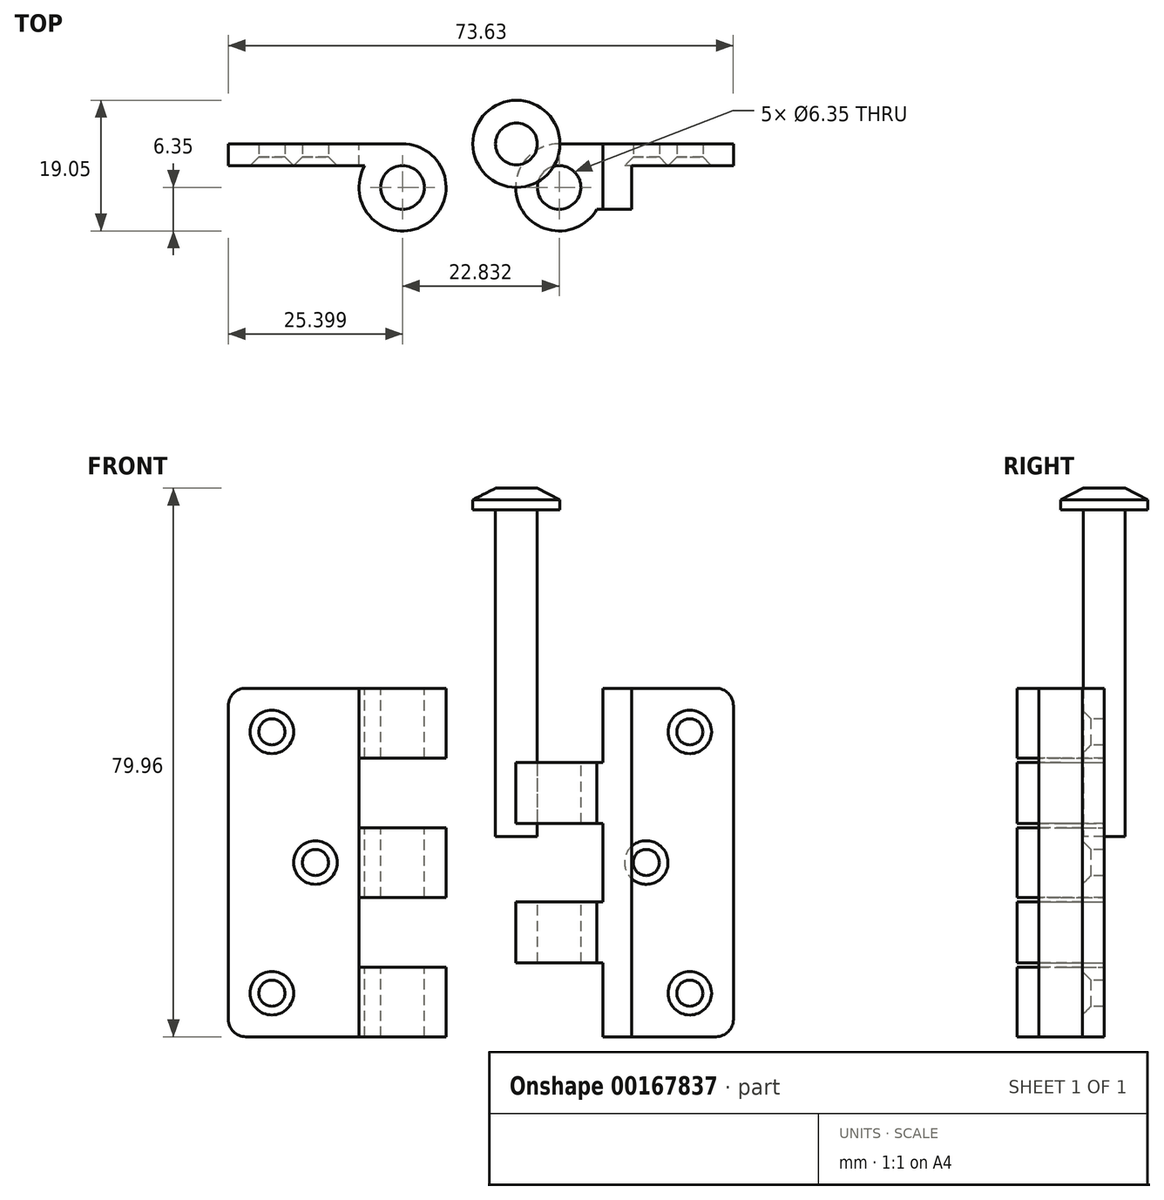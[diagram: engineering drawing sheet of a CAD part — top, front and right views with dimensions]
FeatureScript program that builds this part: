
annotation { "Feature Type Name" : "Feature", "Feature Type Description" : "" }
export const myFeature = defineFeature(function(context is Context, id is Id, definition is map)
    precondition{}
    {
        {
            var Q0;
            Q0=qCreatedBy(makeId("Front.planeOp"),FACE);
            var sketch = newSketch(context, id + "F0", { "sketchPlane" : qUnion([Q0])});
            skLineSegment(sketch, "E0.bottom", {"start": v(-44.61, 38.03) * mm, "end": v(-19.21, 38.03) * mm});
            skLineSegment(sketch, "E0.top", {"start": v(-44.61, -12.77) * mm, "end": v(-19.21, -12.77) * mm});
            skLineSegment(sketch, "E0.left", {"start": v(-44.61, 38.03) * mm, "end": v(-44.61, -12.77) * mm});
            skLineSegment(sketch, "E0.right", {"start": v(-19.21, 38.03) * mm, "end": v(-19.21, -12.77) * mm});
            skSolve(sketch);
        }
        {
            var Q0;
            Q0=qSketchRegion(id+"F0",true);
            extrude(context, id + "F1", {"entities" : qUnion([Q0]), "depth" : 3.17 * mm});
        }
        {
            var Q0;
            Q0=makeQuery(id+"F1.opExtrude","SWEPT_FACE",FACE,{"disambiguationData":[OSD([sQuery(id+"F0.wireOp",EDGE,"E0.bottom")])]});
            var sketch = newSketch(context, id + "F2", { "sketchPlane" : qUnion([Q0])});
            skCircle(sketch, "E1", {"center": v(-19.21, -6.35) * mm, "radius": 6.35 * mm});
            skCircle(sketch, "E2", {"center": v(-19.21, -6.35) * mm, "radius": 3.18 * mm});
            skSolve(sketch);
        }
        {
            var Q0;
            {var subQ5=sQuery(id+"F2.wireOp",EDGE,"E2");Q0=makeQuery(id+"F2.imprint","IMPRINT",FACE,{"disambiguationData":[TD([[makeQuery(id+"F2.imprint","IMPRINT",EDGE,{"derivedFrom":subQ5}),-1.0]])]});}
            var Q1;
            {var subQ1=sQuery(id+"F0.wireOp",EDGE,"E0.bottom");var subQ2=makeQuery(id+"F1.opExtrude","SWEPT_EDGE",EDGE,{"disambiguationData":[OSD([subQ1,sQuery(id+"F0.wireOp",EDGE,"E0.right")])]});Q1=makeQuery(id+"F2.imprint","IMPRINT",FACE,{"disambiguationData":[TD([[makeQuery(id+"F2.imprint","IMPRINT",EDGE,{"derivedFrom":subQ2}),1.0]])]});}
            var Q2;
            Q2=makeQuery(id+"F1.opExtrude","SWEPT_FACE",FACE,{"disambiguationData":[OSD([sQuery(id+"F0.wireOp",EDGE,"E0.top")])]});
            extrude(context, id + "F3", {"entities" : qUnion([Q0, Q1]), "operationType" : NewBodyOperationType.ADD, "endBound" : BoundingType.UP_TO_SURFACE, "oppositeDirection" : true, "endBoundEntityFace" : qUnion([Q2]), "depth" : 25.4 * mm});
        }
        {
            var Q0;
            Q0=makeQuery(id+"F1.opExtrude","CAP_FACE",FACE,{"disambiguationData":[OSD([sQuery(id+"F0.wireOp",EDGE,"E0.bottom"),sQuery(id+"F0.wireOp",EDGE,"E0.top"),sQuery(id+"F0.wireOp",EDGE,"E0.left"),sQuery(id+"F0.wireOp",EDGE,"E0.right")])],"isStart":false});
            var sketch = newSketch(context, id + "F4", { "sketchPlane" : qUnion([Q0])});
            skLineSegment(sketch, "E3", {"start": v(-34.66, 38.03) * mm, "end": v(-34.66, -12.77) * mm, "construction": true});
            skLineSegment(sketch, "E4", {"start": v(-24.7, 12.63) * mm, "end": v(-44.61, 12.63) * mm, "construction": true});
            skLineSegment(sketch, "E5", {"start": v(-24.7, -6.42) * mm, "end": v(-44.61, -6.42) * mm, "construction": true});
            skLineSegment(sketch, "E6", {"start": v(-24.7, 31.68) * mm, "end": v(-44.61, 31.68) * mm, "construction": true});
            skPoint(sketch, "E7", {"position": v(-38.26, 31.68) * mm});
            skPoint(sketch, "E8", {"position": v(-31.91, 12.63) * mm});
            skPoint(sketch, "E9", {"position": v(-38.26, -6.42) * mm});
            skSolve(sketch);
        }
        {
            var Q0;
            Q0=makeQuery(id+"F1.opExtrude","SWEPT_EDGE",EDGE,{"disambiguationData":[OSD([sQuery(id+"F0.wireOp",EDGE,"E0.bottom"),sQuery(id+"F0.wireOp",EDGE,"E0.left")])]});
            var Q1;
            Q1=makeQuery(id+"F1.opExtrude","SWEPT_EDGE",EDGE,{"disambiguationData":[OSD([sQuery(id+"F0.wireOp",EDGE,"E0.top"),sQuery(id+"F0.wireOp",EDGE,"E0.left")])]});
            fillet(context, id + "F5", {"entities" : qUnion([Q0, Q1]), "radius" : 2.54 * mm, "tangentPropagation" : true, "allowEdgeOverflow" : false});
        }
        {
            var Q0;
            Q0=makeQuery(id+"F0.imprint","IMPRINT",FACE,{"disambiguationData":[TD([[makeQuery(id+"F0.imprint","IMPRINT",EDGE,{"derivedFrom":sQuery(id+"F0.wireOp",EDGE,"E0.bottom")}),-1.0]])]});
            var sketch = newSketch(context, id + "F6", { "sketchPlane" : qUnion([Q0])});
            skLineSegment(sketch, "E10", {"start": v(-25.56, -2.61) * mm, "end": v(-12.86, -2.61) * mm});
            skLineSegment(sketch, "E11", {"start": v(-12.86, -2.61) * mm, "end": v(-12.86, 7.55) * mm});
            skLineSegment(sketch, "E12", {"start": v(-12.86, 7.55) * mm, "end": v(-25.56, 7.55) * mm});
            skLineSegment(sketch, "E13", {"start": v(-25.56, 7.55) * mm, "end": v(-25.56, -2.61) * mm});
            skLineSegment(sketch, "E14", {"start": v(-25.56, 17.7) * mm, "end": v(-12.86, 17.7) * mm});
            skLineSegment(sketch, "E15", {"start": v(-12.86, 17.7) * mm, "end": v(-12.86, 27.87) * mm});
            skLineSegment(sketch, "E16", {"start": v(-12.86, 27.87) * mm, "end": v(-25.56, 27.87) * mm});
            skLineSegment(sketch, "E17", {"start": v(-25.56, 27.87) * mm, "end": v(-25.56, 17.7) * mm});
            skPoint(sketch, "E18", {"position": v(-19.21, -2.61) * mm});
            skLineSegment(sketch, "E19", {"start": v(-19.21, 27.87) * mm, "end": v(-19.21, 38.03) * mm});
            skLineSegment(sketch, "E20", {"start": v(-19.21, 17.7) * mm, "end": v(-19.21, 7.55) * mm});
            skLineSegment(sketch, "E21", {"start": v(-19.21, -2.61) * mm, "end": v(-19.21, -12.77) * mm});
            skLineSegment(sketch, "E22", {"start": v(-12.86, 17.7) * mm, "end": v(-12.86, 7.55) * mm});
            skLineSegment(sketch, "E23", {"start": v(-25.56, 7.55) * mm, "end": v(-25.56, 17.7) * mm});
            skLineSegment(sketch, "E24", {"start": v(-25.56, 27.87) * mm, "end": v(-25.56, 38.04) * mm});
            skLineSegment(sketch, "E25", {"start": v(-25.56, 38.04) * mm, "end": v(-12.86, 38.03) * mm});
            skLineSegment(sketch, "E26", {"start": v(-12.86, 38.03) * mm, "end": v(-12.86, 27.87) * mm});
            skLineSegment(sketch, "E27", {"start": v(-12.86, -2.61) * mm, "end": v(-12.86, -12.77) * mm});
            skLineSegment(sketch, "E28", {"start": v(-12.86, -12.77) * mm, "end": v(-25.56, -12.77) * mm});
            skLineSegment(sketch, "E29", {"start": v(-25.56, -12.77) * mm, "end": v(-25.56, -2.61) * mm});
            skSolve(sketch);
        }
        {
            var Q0;
            {var subQ0=sQuery(id+"F6.wireOp",EDGE,"E17");Q0=makeQuery(id+"F6.imprint","IMPRINT",FACE,{"disambiguationData":[TD([[makeQuery(id+"F6.imprint","IMPRINT",EDGE,{"derivedFrom":subQ0}),1.0]])]});}
            var Q1;
            {var subQ0=sQuery(id+"F6.wireOp",EDGE,"E15");Q1=makeQuery(id+"F6.imprint","IMPRINT",FACE,{"disambiguationData":[TD([[makeQuery(id+"F6.imprint","IMPRINT",EDGE,{"derivedFrom":subQ0}),1.0]])]});}
            var Q2;
            {var subQ0=sQuery(id+"F6.wireOp",EDGE,"E13");Q2=makeQuery(id+"F6.imprint","IMPRINT",FACE,{"disambiguationData":[TD([[makeQuery(id+"F6.imprint","IMPRINT",EDGE,{"derivedFrom":subQ0}),1.0]])]});}
            var Q3;
            {var subQ0=sQuery(id+"F6.wireOp",EDGE,"E11");Q3=makeQuery(id+"F6.imprint","IMPRINT",FACE,{"disambiguationData":[TD([[makeQuery(id+"F6.imprint","IMPRINT",EDGE,{"derivedFrom":subQ0}),1.0]])]});}
            extrude(context, id + "F7", {"entities" : qUnion([Q0, Q1, Q2, Q3]), "operationType" : NewBodyOperationType.REMOVE, "depth" : 25.4 * mm});
        }
        {
            var Q0;
            Q0=qCreatedBy(makeId("Front.planeOp"),FACE);
            var sketch = newSketch(context, id + "F8", { "sketchPlane" : qUnion([Q0])});
            skLineSegment(sketch, "E30.bottom", {"start": v(3.62, 38.03) * mm, "end": v(29.02, 38.03) * mm});
            skLineSegment(sketch, "E30.top", {"start": v(3.62, -12.77) * mm, "end": v(29.02, -12.77) * mm});
            skLineSegment(sketch, "E30.left", {"start": v(3.62, 38.03) * mm, "end": v(3.62, -12.77) * mm});
            skLineSegment(sketch, "E30.right", {"start": v(29.02, 38.03) * mm, "end": v(29.02, -12.77) * mm});
            skSolve(sketch);
        }
        {
            var Q0;
            Q0=qSketchRegion(id+"F8",true);
            extrude(context, id + "F9", {"entities" : qUnion([Q0]), "depth" : 3.17 * mm});
        }
        {
            var Q0;
            Q0=makeQuery(id+"F9.opExtrude","SWEPT_FACE",FACE,{"disambiguationData":[OSD([sQuery(id+"F8.wireOp",EDGE,"E30.bottom")])]});
            var sketch = newSketch(context, id + "F10", { "sketchPlane" : qUnion([Q0])});
            skCircle(sketch, "E31", {"center": v(3.62, -6.35) * mm, "radius": 6.35 * mm});
            skLineSegment(sketch, "E32", {"start": v(-33.9, -6.35) * mm, "end": v(23.07, -6.35) * mm, "construction": true});
            skCircle(sketch, "E33", {"center": v(3.62, -6.35) * mm, "radius": 3.18 * mm});
            skPoint(sketch, "E34.endSnap0", {"position": v(16.32, -3.18) * mm});
            skLineSegment(sketch, "E35", {"start": v(9.12, -3.18) * mm, "end": v(14.2, -3.18) * mm});
            skLineSegment(sketch, "E36", {"start": v(14.2, -3.18) * mm, "end": v(14.2, -9.53) * mm});
            skLineSegment(sketch, "E37", {"start": v(14.2, -9.53) * mm, "end": v(9.12, -9.53) * mm});
            skArc(sketch, "E38", {"start": v(9.12, -9.53) * mm, "mid": v(9.97, -6.35) * mm, "end": v(9.12, -3.17) * mm});
            skSolve(sketch);
        }
        {
            var Q0;
            {var subQ5=sQuery(id+"F10.wireOp",EDGE,"E33");Q0=makeQuery(id+"F10.imprint","IMPRINT",FACE,{"disambiguationData":[TD([[makeQuery(id+"F10.imprint","IMPRINT",EDGE,{"derivedFrom":subQ5}),-1.0]])]});}
            var Q1;
            {var subQ1=sQuery(id+"F8.wireOp",EDGE,"E30.bottom");var subQ2=makeQuery(id+"F9.opExtrude","SWEPT_EDGE",EDGE,{"disambiguationData":[OSD([subQ1,sQuery(id+"F8.wireOp",EDGE,"E30.left")])]});Q1=makeQuery(id+"F10.imprint","IMPRINT",FACE,{"disambiguationData":[TD([[makeQuery(id+"F10.imprint","IMPRINT",EDGE,{"derivedFrom":subQ2}),-1.0]])]});}
            var Q2;
            {var subQ0=sQuery(id+"F10.wireOp",EDGE,"E35");Q2=makeQuery(id+"F10.imprint","IMPRINT",FACE,{"disambiguationData":[TD([[makeQuery(id+"F10.imprint","IMPRINT",EDGE,{"derivedFrom":subQ0}),-1.0]])]});}
            var Q3;
            Q3=makeQuery(id+"F9.opExtrude","SWEPT_FACE",FACE,{"disambiguationData":[OSD([sQuery(id+"F8.wireOp",EDGE,"E30.top")])]});
            extrude(context, id + "F11", {"entities" : qUnion([Q0, Q1, Q2]), "operationType" : NewBodyOperationType.ADD, "endBound" : BoundingType.UP_TO_SURFACE, "oppositeDirection" : true, "endBoundEntityFace" : qUnion([Q3]), "depth" : 25.4 * mm});
        }
        {
            var Q0;
            Q0=makeQuery(id+"F9.opExtrude","CAP_FACE",FACE,{"disambiguationData":[OSD([sQuery(id+"F8.wireOp",EDGE,"E30.bottom"),sQuery(id+"F8.wireOp",EDGE,"E30.top"),sQuery(id+"F8.wireOp",EDGE,"E30.left"),sQuery(id+"F8.wireOp",EDGE,"E30.right")])],"isStart":true});
            var sketch = newSketch(context, id + "F12", { "sketchPlane" : qUnion([Q0])});
            skLineSegment(sketch, "E39", {"start": v(-9.97, 27.23) * mm, "end": v(2.73, 27.23) * mm});
            skLineSegment(sketch, "E40", {"start": v(2.73, 27.23) * mm, "end": v(2.73, 38.03) * mm});
            skLineSegment(sketch, "E41", {"start": v(2.73, 38.03) * mm, "end": v(-9.97, 38.03) * mm});
            skLineSegment(sketch, "E42", {"start": v(-9.97, 27.23) * mm, "end": v(-9.97, 38.03) * mm});
            skLineSegment(sketch, "E43", {"start": v(-9.97, 27.23) * mm, "end": v(-9.97, -12.77) * mm});
            skLineSegment(sketch, "E44", {"start": v(-9.97, -12.77) * mm, "end": v(2.73, -12.77) * mm});
            skLineSegment(sketch, "E45", {"start": v(2.73, -12.77) * mm, "end": v(2.73, 27.23) * mm});
            skLineSegment(sketch, "E46", {"start": v(2.73, 18.34) * mm, "end": v(-9.97, 18.34) * mm});
            skLineSegment(sketch, "E47", {"start": v(-9.97, 6.91) * mm, "end": v(2.73, 6.91) * mm});
            skLineSegment(sketch, "E48", {"start": v(-9.97, -1.98) * mm, "end": v(2.73, -1.98) * mm});
            skSolve(sketch);
        }
        {
            var Q0;
            {var subQ0=sQuery(id+"F12.wireOp",EDGE,"E40");Q0=makeQuery(id+"F12.imprint","IMPRINT",FACE,{"disambiguationData":[TD([[makeQuery(id+"F12.imprint","IMPRINT",EDGE,{"derivedFrom":subQ0}),1.0]])]});}
            var Q1;
            {var subQ0=sQuery(id+"F12.wireOp",EDGE,"E42");Q1=makeQuery(id+"F12.imprint","IMPRINT",FACE,{"disambiguationData":[TD([[makeQuery(id+"F12.imprint","IMPRINT",EDGE,{"derivedFrom":subQ0}),-1.0]])]});}
            var Q2;
            {var subQ0=sQuery(id+"F12.wireOp",EDGE,"E46");var subQ1=sQuery(id+"F12.wireOp",EDGE,"E43");var subQ2=makeQuery(id+"F12.imprint","INTERSECT",VERTEX,{"derivedFrom":[subQ1,subQ0]});Q2=makeQuery(id+"F12.imprint","IMPRINT",FACE,{"disambiguationData":[TD([[makeQuery(id+"F12.imprint","IMPRINT",EDGE,{"disambiguationData":[TD([[subQ2,-1.0]])],"derivedFrom":subQ1}),1.0]])]});}
            var Q3;
            {var subQ0=sQuery(id+"F12.wireOp",EDGE,"E46");var subQ1=sQuery(id+"F12.wireOp",EDGE,"E45");var subQ2=makeQuery(id+"F12.imprint","INTERSECT",VERTEX,{"derivedFrom":[subQ1,subQ0]});Q3=makeQuery(id+"F12.imprint","IMPRINT",FACE,{"disambiguationData":[TD([[makeQuery(id+"F12.imprint","IMPRINT",EDGE,{"disambiguationData":[TD([[subQ2,1.0]])],"derivedFrom":subQ1}),1.0]])]});}
            var Q4;
            {var subQ0=sQuery(id+"F12.wireOp",EDGE,"E44");var subQ3=sQuery(id+"F12.wireOp",EDGE,"E45");var subQ4=makeQuery(id+"F12.imprint","INTERSECT",VERTEX,{"derivedFrom":[subQ0,subQ3]});Q4=makeQuery(id+"F12.imprint","IMPRINT",FACE,{"disambiguationData":[TD([[makeQuery(id+"F12.imprint","IMPRINT",EDGE,{"disambiguationData":[TD([[subQ4,1.0]])],"derivedFrom":subQ0}),1.0]])]});}
            var Q5;
            {var subQ1=sQuery(id+"F12.wireOp",EDGE,"E43");var subQ3=sQuery(id+"F12.wireOp",EDGE,"E48");var subQ4=makeQuery(id+"F12.imprint","INTERSECT",VERTEX,{"derivedFrom":[subQ1,subQ3]});Q5=makeQuery(id+"F12.imprint","IMPRINT",FACE,{"disambiguationData":[TD([[makeQuery(id+"F12.imprint","IMPRINT",EDGE,{"disambiguationData":[TD([[subQ4,-1.0]])],"derivedFrom":subQ3}),-1.0]])]});}
            extrude(context, id + "F13", {"entities" : qUnion([Q0, Q1, Q2, Q3, Q4, Q5]), "operationType" : NewBodyOperationType.REMOVE, "oppositeDirection" : true, "depth" : 25.4 * mm});
        }
        {
            var Q0;
            Q0=qCreatedBy(makeId("Front.planeOp"),FACE);
            var sketch = newSketch(context, id + "F14", { "sketchPlane" : qUnion([Q0])});
            skLineSegment(sketch, "E49", {"start": v(-5.65, 64.02) * mm, "end": v(-5.65, 16.4) * mm});
            skLineSegment(sketch, "E50", {"start": v(-5.65, 16.4) * mm, "end": v(-2.6, 16.4) * mm});
            skLineSegment(sketch, "E51", {"start": v(-2.6, 16.4) * mm, "end": v(-2.6, 67.2) * mm});
            skLineSegment(sketch, "E52", {"start": v(-2.6, 67.2) * mm, "end": v(-5.65, 67.2) * mm});
            skLineSegment(sketch, "E53", {"start": v(-5.65, 67.2) * mm, "end": v(-8.96, 65.52) * mm});
            skLineSegment(sketch, "E54", {"start": v(-8.96, 65.52) * mm, "end": v(-8.96, 64.02) * mm});
            skLineSegment(sketch, "E55", {"start": v(-8.96, 64.02) * mm, "end": v(-5.65, 64.02) * mm});
            skSolve(sketch);
        }
        {
            var Q0;
            Q0=qSketchRegion(id+"F14",true);
            var Q1;
            Q1=sQuery(id+"F14.wireOp",EDGE,"E51");
            revolve(context, id + "F15", {"entities" : qUnion([Q0]), "axis" : qUnion([Q1]), "revolveType" : RevolveType.FULL});
        }
        {
            var Q0;
            Q0=makeQuery(id+"F9.opExtrude","CAP_FACE",FACE,{"disambiguationData":[OSD([sQuery(id+"F8.wireOp",EDGE,"E30.bottom"),sQuery(id+"F8.wireOp",EDGE,"E30.top"),sQuery(id+"F8.wireOp",EDGE,"E30.left"),sQuery(id+"F8.wireOp",EDGE,"E30.right")])],"isStart":false});
            var sketch = newSketch(context, id + "F16", { "sketchPlane" : qUnion([Q0])});
            skLineSegment(sketch, "E56", {"start": v(21.6, 38.03) * mm, "end": v(21.6, -12.77) * mm, "construction": true});
            skLineSegment(sketch, "E57", {"start": v(9.97, 12.63) * mm, "end": v(29.02, 12.63) * mm, "construction": true});
            skPoint(sketch, "E58", {"position": v(16.32, 12.63) * mm});
            skPoint(sketch, "E59", {"position": v(22.67, 31.68) * mm});
            skPoint(sketch, "E60", {"position": v(22.67, -6.42) * mm});
            skSolve(sketch);
        }
        {
            var Q0;
            Q0=sQuery(id+"F4.wireOp",VERTEX,"E7");
            var Q1;
            Q1=sQuery(id+"F4.wireOp",VERTEX,"E8");
            var Q2;
            Q2=sQuery(id+"F4.wireOp",VERTEX,"E9");
            var Q3;
            Q3=makeQuery(id+"F1.opExtrude","SWEPT_BODY",BODY,{"disambiguationData":[OSD([sQuery(id+"F0.wireOp",EDGE,"E0.bottom"),sQuery(id+"F0.wireOp",EDGE,"E0.top"),sQuery(id+"F0.wireOp",EDGE,"E0.left"),sQuery(id+"F0.wireOp",EDGE,"E0.right")])]});
            hole(context, id + "F17", {"style" : HoleStyle.C_SINK, "endStyle" : HoleEndStyle.THROUGH, "holeDiameter" : 3.8 * mm, "cSinkDiameter" : 6.35 * mm, "cSinkAngle" : 90 * degree, "locations" : qUnion([Q0, Q1, Q2]), "scope" : qUnion([Q3]), "isTappedThrough" : true});
        }
        {
            var Q0;
            Q0=sQuery(id+"F16.wireOp",VERTEX,"E59");
            var Q1;
            Q1=sQuery(id+"F16.wireOp",VERTEX,"E58");
            var Q2;
            Q2=sQuery(id+"F16.wireOp",VERTEX,"E60");
            var Q3;
            Q3=makeQuery(id+"F9.opExtrude","SWEPT_BODY",BODY,{"disambiguationData":[OSD([sQuery(id+"F8.wireOp",EDGE,"E30.bottom"),sQuery(id+"F8.wireOp",EDGE,"E30.top"),sQuery(id+"F8.wireOp",EDGE,"E30.left"),sQuery(id+"F8.wireOp",EDGE,"E30.right")])]});
            hole(context, id + "F18", {"style" : HoleStyle.C_SINK, "endStyle" : HoleEndStyle.THROUGH, "holeDiameter" : 3.8 * mm, "cSinkDiameter" : 6.35 * mm, "cSinkAngle" : 90 * degree, "locations" : qUnion([Q0, Q1, Q2]), "scope" : qUnion([Q3]), "isTappedThrough" : true});
        }
        {
            var Q0;
            Q0=makeQuery(id+"F9.opExtrude","SWEPT_EDGE",EDGE,{"disambiguationData":[OSD([sQuery(id+"F8.wireOp",EDGE,"E30.bottom"),sQuery(id+"F8.wireOp",EDGE,"E30.right")])]});
            var Q1;
            Q1=makeQuery(id+"F9.opExtrude","SWEPT_EDGE",EDGE,{"disambiguationData":[OSD([sQuery(id+"F8.wireOp",EDGE,"E30.top"),sQuery(id+"F8.wireOp",EDGE,"E30.right")])]});
            fillet(context, id + "F19", {"entities" : qUnion([Q0, Q1]), "radius" : 2.54 * mm, "tangentPropagation" : true, "allowEdgeOverflow" : false});
        }
    });
